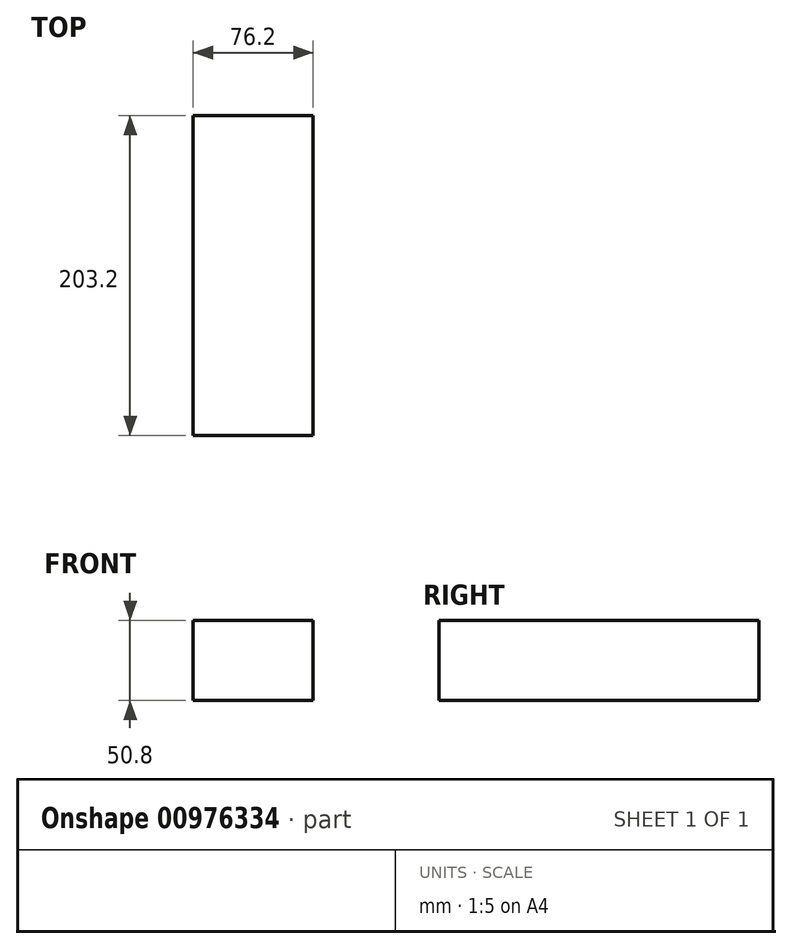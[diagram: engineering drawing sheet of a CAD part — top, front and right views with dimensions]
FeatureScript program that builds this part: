
annotation { "Feature Type Name" : "Feature", "Feature Type Description" : "" }
export const myFeature = defineFeature(function(context is Context, id is Id, definition is map)
    precondition{}
    {
        {
            var Q0;
            Q0=qCreatedBy(makeId("Right.planeOp"),FACE);
            var sketch = newSketch(context, id + "F0", { "sketchPlane" : qUnion([Q0])});
            skLineSegment(sketch, "E0.bottom", {"start": v(105.39, 10.83) * mm, "end": v(-97.81, 10.83) * mm});
            skLineSegment(sketch, "E0.top", {"start": v(105.39, -39.97) * mm, "end": v(-97.81, -39.97) * mm});
            skLineSegment(sketch, "E0.left", {"start": v(105.39, 10.83) * mm, "end": v(105.39, -39.97) * mm});
            skLineSegment(sketch, "E0.right", {"start": v(-97.81, 10.83) * mm, "end": v(-97.81, -39.97) * mm});
            skSolve(sketch);
        }
        {
            var Q0;
            Q0=makeQuery(id+"F0.imprint","IMPRINT",FACE,{"disambiguationData":[TD([[makeQuery(id+"F0.imprint","IMPRINT",EDGE,{"derivedFrom":sQuery(id+"F0.wireOp",EDGE,"E0.bottom")}),1.0]])]});
            extrude(context, id + "F1", {"entities" : qUnion([Q0]), "depth" : 76.2 * mm, "offsetDistance" : 25.4 * mm});
        }
    });
